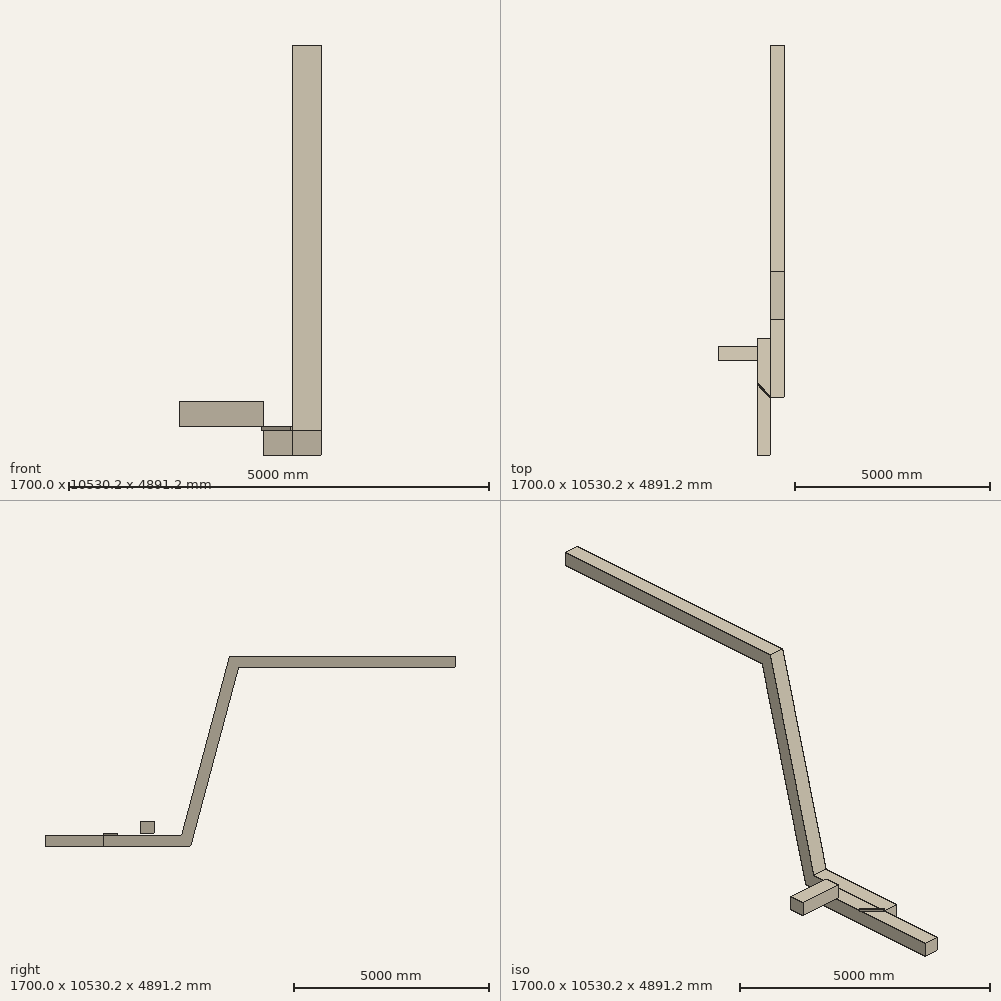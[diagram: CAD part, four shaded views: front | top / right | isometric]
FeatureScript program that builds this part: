
annotation { "Feature Type Name" : "Feature", "Feature Type Description" : "" }
export const myFeature = defineFeature(function(context is Context, id is Id, definition is map)
    precondition{}
    {
        {
            var Q0;
            Q0=qCreatedBy(makeId("Right.planeOp"),FACE);
            var sketch = newSketch(context, id + "F0", { "sketchPlane" : qUnion([Q0])});
            skLineSegment(sketch, "E0", {"start": v(0, 0) * mm, "end": v(0, 300) * mm});
            skLineSegment(sketch, "E1", {"start": v(0, 300) * mm, "end": v(2000, 300) * mm});
            skLineSegment(sketch, "E2", {"start": v(2230.2, 0) * mm, "end": v(0, 0) * mm});
            skLineSegment(sketch, "E3", {"start": v(2000, 300) * mm, "end": v(3230.2, 4891.16) * mm});
            skLineSegment(sketch, "E4", {"start": v(3230.2, 4891.16) * mm, "end": v(9030.2, 4891.16) * mm});
            skLineSegment(sketch, "E5", {"start": v(9030.2, 4891.16) * mm, "end": v(9030.2, 4591.16) * mm});
            skLineSegment(sketch, "E6", {"start": v(2230.2, 0) * mm, "end": v(3460.4, 4591.16) * mm});
            skLineSegment(sketch, "E7", {"start": v(3460.4, 4591.16) * mm, "end": v(9030.2, 4591.16) * mm});
            skSolve(sketch);
        }
        {
            var Q0;
            Q0 = qSketchRegion(id + "F0", true);
            extrude(context, id + "F1", {"entities" : qUnion([Q0]), "oppositeDirection" : true, "depth" : 350 * mm, "offsetDistance" : 25 * mm});
        }
        {
            var Q0;
            Q0=makeQuery(id+"F1.opExtrude","CAP_FACE",FACE,{"disambiguationData":[OSD([sQuery(id+"F0.wireOp",EDGE,"E0"),sQuery(id+"F0.wireOp",EDGE,"E1"),sQuery(id+"F0.wireOp",EDGE,"E2"),sQuery(id+"F0.wireOp",EDGE,"E3"),sQuery(id+"F0.wireOp",EDGE,"E4"),sQuery(id+"F0.wireOp",EDGE,"E5"),sQuery(id+"F0.wireOp",EDGE,"E6"),sQuery(id+"F0.wireOp",EDGE,"E7")])],"isStart":false});
            var sketch = newSketch(context, id + "F2", { "sketchPlane" : qUnion([Q0])});
            skPoint(sketch, "E8.oppositeSnap0", {"position": v(-1115.1, 0) * mm});
            skLineSegment(sketch, "E8.bottom", {"start": v(-1500, 300) * mm, "end": v(1500, 300) * mm});
            skLineSegment(sketch, "E8.top", {"start": v(-1500, 0) * mm, "end": v(1500, 0) * mm});
            skLineSegment(sketch, "E8.left", {"start": v(-1500, 300) * mm, "end": v(-1500, 0) * mm});
            skLineSegment(sketch, "E8.right", {"start": v(1500, 300) * mm, "end": v(1500, 0) * mm});
            skSolve(sketch);
        }
        {
            var Q0;
            Q0 = qSketchRegion(id + "F2", true);
            extrude(context, id + "F3", {"entities" : qUnion([Q0]), "depth" : 350 * mm, "offsetDistance" : 25 * mm});
        }
        {
            var Q0;
            Q0=makeQuery(id+"F3.opExtrude","CAP_FACE",FACE,{"disambiguationData":[OSD([sQuery(id+"F2.wireOp",EDGE,"E8.bottom"),sQuery(id+"F2.wireOp",EDGE,"E8.top"),sQuery(id+"F2.wireOp",EDGE,"E8.left"),sQuery(id+"F2.wireOp",EDGE,"E8.right")])],"isStart":false});
            var sketch = newSketch(context, id + "F4", { "sketchPlane" : qUnion([Q0])});
            skLineSegment(sketch, "E9.bottom", {"start": v(-1300, 650) * mm, "end": v(-950, 650) * mm});
            skLineSegment(sketch, "E9.top", {"start": v(-1300, 350) * mm, "end": v(-950, 350) * mm});
            skLineSegment(sketch, "E9.left", {"start": v(-1300, 650) * mm, "end": v(-1300, 350) * mm});
            skLineSegment(sketch, "E9.right", {"start": v(-950, 650) * mm, "end": v(-950, 350) * mm});
            skSolve(sketch);
        }
        {
            var Q0;
            Q0 = qSketchRegion(id + "F4", true);
            extrude(context, id + "F5", {"entities" : qUnion([Q0]), "depth" : 1000 * mm, "offsetDistance" : 25 * mm});
        }
        {
            var Q0;
            Q0=makeQuery(id+"F3.opExtrude","SWEPT_FACE",FACE,{"disambiguationData":[OSD([sQuery(id+"F2.wireOp",EDGE,"E8.bottom")])]});
            var sketch = newSketch(context, id + "F6", { "sketchPlane" : qUnion([Q0])});
            skLineSegment(sketch, "E10", {"start": v(-350, 0) * mm, "end": v(-700, 357.07) * mm});
            skLineSegment(sketch, "E11", {"start": v(-700, 357.07) * mm, "end": v(-714.28, 343.07) * mm});
            skLineSegment(sketch, "E12", {"start": v(-714.28, 343.07) * mm, "end": v(-378, 0) * mm});
            skLineSegment(sketch, "E13", {"start": v(-378, 0) * mm, "end": v(-350, 0) * mm});
            skSolve(sketch);
        }
        {
            var Q0;
            Q0 = qSketchRegion(id + "F6", true);
            extrude(context, id + "F7", {"entities" : qUnion([Q0]), "depth" : 50 * mm, "offsetDistance" : 25 * mm});
        }
    });
